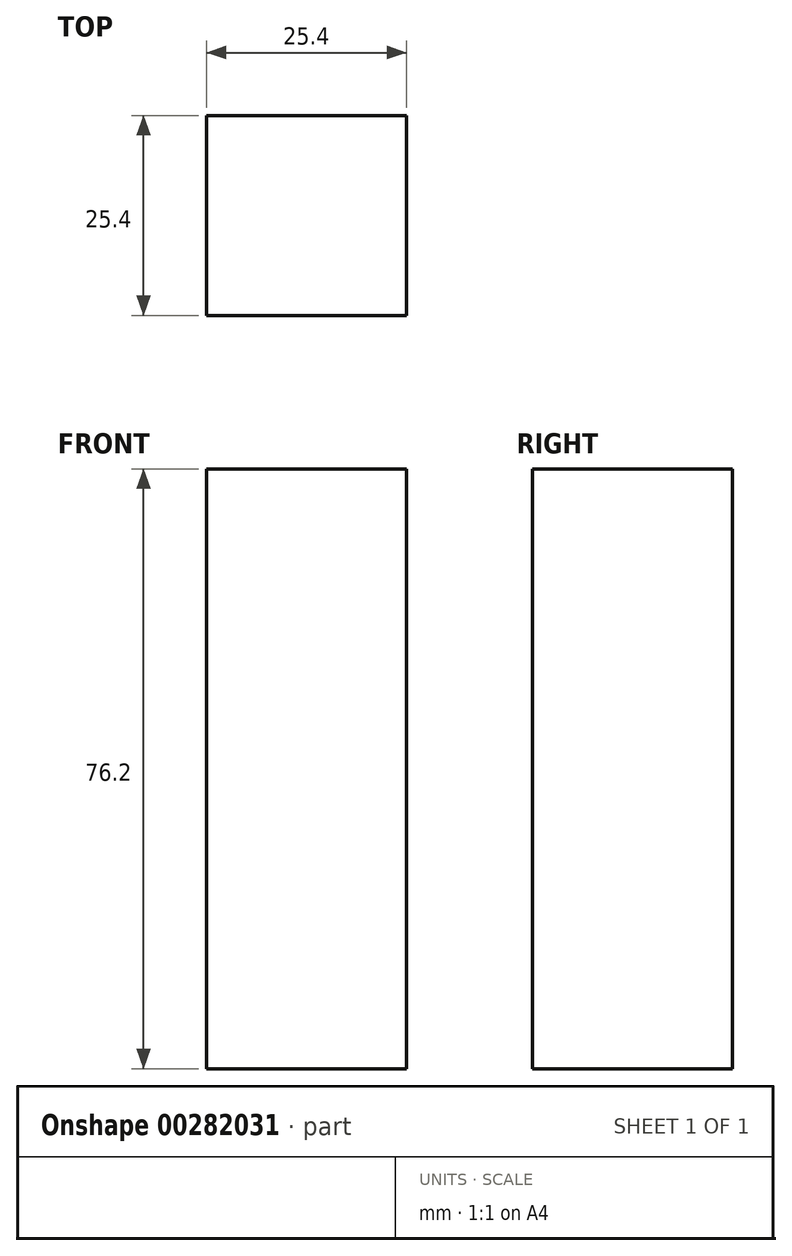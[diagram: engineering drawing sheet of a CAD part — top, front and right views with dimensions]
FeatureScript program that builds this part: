
annotation { "Feature Type Name" : "Feature", "Feature Type Description" : "" }
export const myFeature = defineFeature(function(context is Context, id is Id, definition is map)
    precondition{}
    {
        {
            var Q0;
            Q0=qCreatedBy(makeId("Front.planeOp"),FACE);
            var sketch = newSketch(context, id + "F0", { "sketchPlane" : qUnion([Q0])});
            skLineSegment(sketch, "E0.bottom", {"start": v(0, 0) * mm, "end": v(-25.4, 0) * mm});
            skLineSegment(sketch, "E0.top", {"start": v(0, 76.2) * mm, "end": v(-25.4, 76.2) * mm});
            skLineSegment(sketch, "E0.left", {"start": v(0, 0) * mm, "end": v(0, 76.2) * mm});
            skLineSegment(sketch, "E0.right", {"start": v(-25.4, 0) * mm, "end": v(-25.4, 76.2) * mm});
            skSolve(sketch);
        }
        {
            var Q0;
            Q0=makeQuery(id+"F0.imprint","IMPRINT",FACE,{"disambiguationData":[TD([[makeQuery(id+"F0.imprint","IMPRINT",EDGE,{"derivedFrom":sQuery(id+"F0.wireOp",EDGE,"E0.bottom")}),-1.0]])]});
            extrude(context, id + "F1", {"entities" : qUnion([Q0]), "depth" : 25.4 * mm});
        }
    });
